# Revit family: AI-Frame-HM-Inset-Double Egress Offset
name_source: partatom
category: Doors
revit_build: Autodesk Revit 2016 (Build: 20150714_1515(x64)
units: mm (PartAtom-declared; Revit-internal decimal feet)

## family parameters
Always vertical = Yes
Cut with Voids When Loaded = No
Room Calculation Point = No
Shared = No
Work Plane-Based = No

## types (2) — shared parameters
Analytic Construction = <None>
Frame Depth = 5 5/8"
Frame Material = <By Category>
Frame Projection = 0"
Frame Recess = 0"
Frame Width = 2"
Frame Width Center Mullion = 2"
Function = Interior
Height = 7' - 0"
Rough Height = 7' - 0 1/2"
Rough Width = 3' - 5"
Shim Space = 1/2"
StopThick = 1/2"
Thickness = 1 3/4"
Width = 3' - 0"

## per-type parameters (varying)
| type | Frame Width at Head Calc | If not what is the frame width at the head | Is the frame the same size all around |
| AI-Frame-HM-Inset-Double Egress Offset | 2" | 4 1/2" | Yes |
| AI-Frame-HM-Inset-Triple Egress Offset 2 | 4" | 4" | No |

## geometry (parser evidence)
native form markers: Blend x2, Sweep x4
no freeform markers — native parametric forms only
